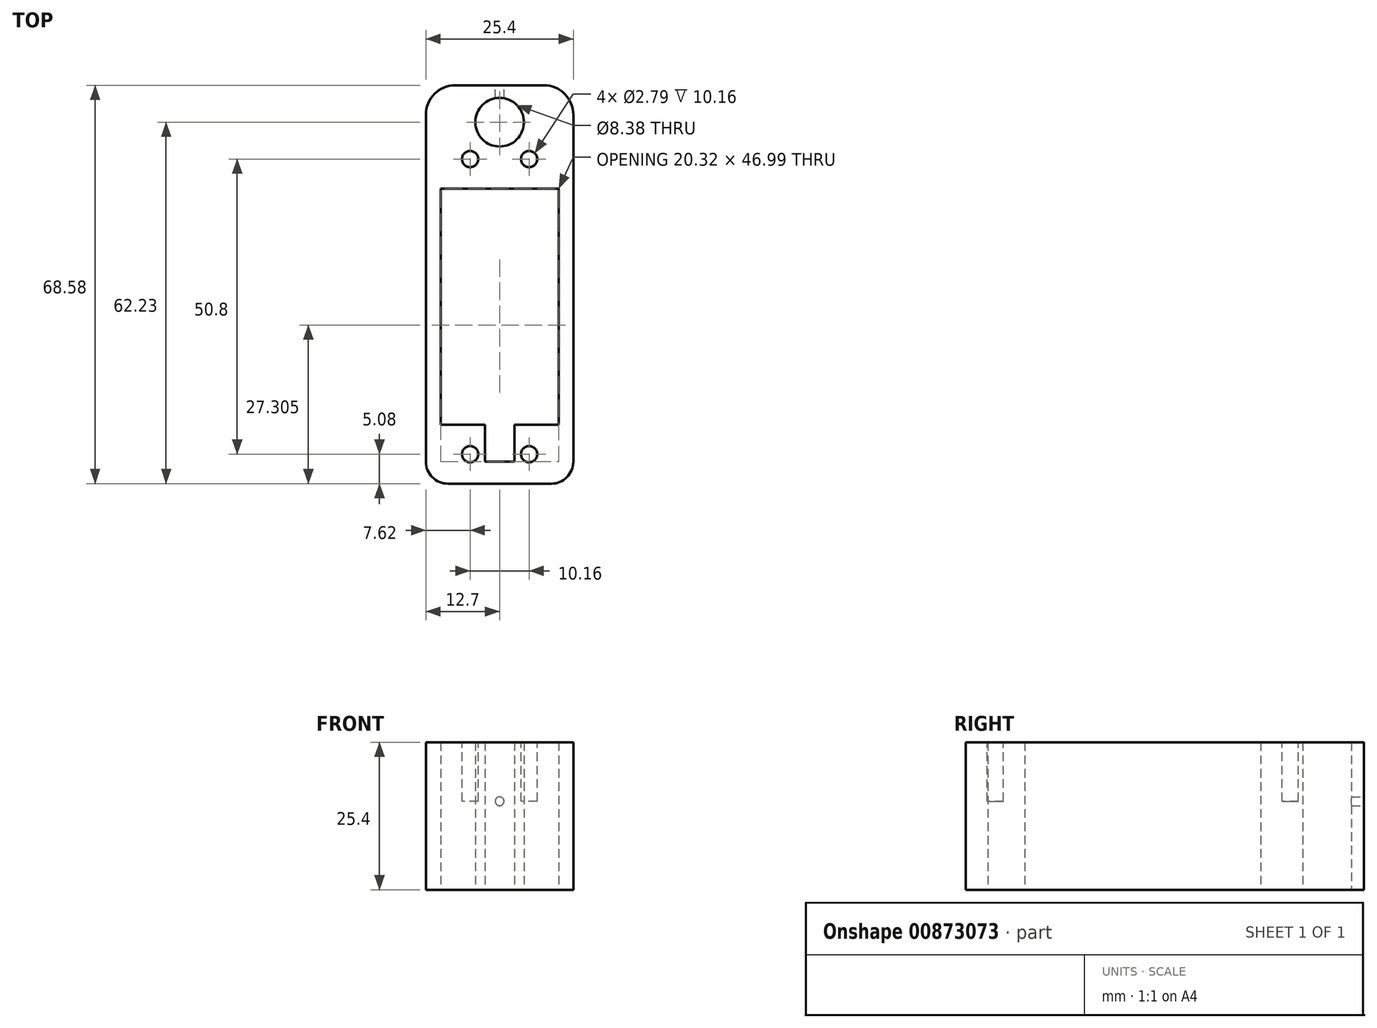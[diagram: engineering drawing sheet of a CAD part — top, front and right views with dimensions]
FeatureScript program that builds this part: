
annotation { "Feature Type Name" : "Feature", "Feature Type Description" : "" }
export const myFeature = defineFeature(function(context is Context, id is Id, definition is map)
    precondition{}
    {
        {
            var Q0;
            Q0=qCreatedBy(makeId("Top.planeOp"),FACE);
            var sketch = newSketch(context, id + "F0", { "sketchPlane" : qUnion([Q0])});
            skLineSegment(sketch, "E0.bottom", {"start": v(-10.16, 0) * mm, "end": v(10.16, 0) * mm});
            skLineSegment(sketch, "E0.top", {"start": v(-10.16, -40.64) * mm, "end": v(10.16, -40.64) * mm});
            skLineSegment(sketch, "E0.left", {"start": v(-10.16, 0) * mm, "end": v(-10.16, -40.64) * mm});
            skLineSegment(sketch, "E0.right", {"start": v(10.16, 0) * mm, "end": v(10.16, -40.64) * mm});
            skLineSegment(sketch, "E1.bottom", {"start": v(-7.62, 17.78) * mm, "end": v(7.62, 17.78) * mm});
            skLineSegment(sketch, "E1.top", {"start": v(-8.9, -50.8) * mm, "end": v(8.9, -50.8) * mm});
            skLineSegment(sketch, "E1.left", {"start": v(-12.7, 12.7) * mm, "end": v(-12.7, -47) * mm});
            skLineSegment(sketch, "E1.right", {"start": v(12.7, 12.7) * mm, "end": v(12.7, -47) * mm});
            skPoint(sketch, "E2", {"position": v(0, 11.43) * mm});
            skCircle(sketch, "E3", {"center": v(0, 11.43) * mm, "radius": 4.2 * mm});
            skPoint(sketch, "E4.visualSharp", {"position": v(-12.7, 17.78) * mm});
            skArc(sketch, "E4.filletArc", {"start": v(-7.62, 17.78) * mm, "mid": v(-11.21, 16.3) * mm, "end": v(-12.7, 12.7) * mm});
            skPoint(sketch, "E5.visualSharp", {"position": v(12.7, 17.78) * mm});
            skArc(sketch, "E5.filletArc", {"start": v(12.7, 12.7) * mm, "mid": v(11.21, 16.3) * mm, "end": v(7.62, 17.78) * mm});
            skPoint(sketch, "E6.visualSharp", {"position": v(12.7, -50.8) * mm});
            skArc(sketch, "E6.filletArc", {"start": v(8.9, -50.8) * mm, "mid": v(11.58, -49.68) * mm, "end": v(12.7, -47) * mm});
            skPoint(sketch, "E7.visualSharp", {"position": v(-12.7, -50.8) * mm});
            skArc(sketch, "E7.filletArc", {"start": v(-12.7, -47) * mm, "mid": v(-11.58, -49.68) * mm, "end": v(-8.9, -50.8) * mm});
            skLineSegment(sketch, "E8.bottom", {"start": v(-2.54, -40.64) * mm, "end": v(2.54, -40.64) * mm});
            skLineSegment(sketch, "E8.top", {"start": v(-2.54, -47) * mm, "end": v(2.54, -47) * mm});
            skLineSegment(sketch, "E8.left", {"start": v(-2.54, -40.64) * mm, "end": v(-2.54, -47) * mm});
            skLineSegment(sketch, "E8.right", {"start": v(2.54, -40.64) * mm, "end": v(2.54, -47) * mm});
            skPoint(sketch, "E9", {"position": v(0, -47) * mm});
            skSolve(sketch);
        }
        {
            var Q0;
            Q0=makeQuery(id+"F0.imprint","IMPRINT",FACE,{"disambiguationData":[TD([[makeQuery(id+"F0.imprint","IMPRINT",EDGE,{"derivedFrom":sQuery(id+"F0.wireOp",EDGE,"E0.bottom")}),1.0]])]});
            extrude(context, id + "F1", {"entities" : qUnion([Q0]), "depth" : 25.4 * mm, "offsetDistance" : 25.4 * mm});
        }
        {
            var Q0;
            Q0=makeQuery(id+"F1.opExtrude","SWEPT_FACE",FACE,{"disambiguationData":[OSD([sQuery(id+"F0.wireOp",EDGE,"E1.bottom")])]});
            var sketch = newSketch(context, id + "F2", { "sketchPlane" : qUnion([Q0])});
            skPoint(sketch, "E10", {"position": v(0, 15.24) * mm});
            skCircle(sketch, "E11", {"center": v(0, 15.24) * mm, "radius": 0.76 * mm});
            skSolve(sketch);
        }
        {
            var Q0;
            Q0=makeQuery(id+"F1.opExtrude","CAP_FACE",FACE,{"disambiguationData":[OSD([sQuery(id+"F0.wireOp",EDGE,"E0.bottom"),sQuery(id+"F0.wireOp",EDGE,"E0.top"),sQuery(id+"F0.wireOp",EDGE,"E0.left"),sQuery(id+"F0.wireOp",EDGE,"E0.right"),sQuery(id+"F0.wireOp",EDGE,"E1.bottom"),sQuery(id+"F0.wireOp",EDGE,"E1.top"),sQuery(id+"F0.wireOp",EDGE,"E1.left"),sQuery(id+"F0.wireOp",EDGE,"E1.right"),sQuery(id+"F0.wireOp",EDGE,"E3"),sQuery(id+"F0.wireOp",EDGE,"E4.filletArc"),sQuery(id+"F0.wireOp",EDGE,"E5.filletArc"),sQuery(id+"F0.wireOp",EDGE,"E6.filletArc"),sQuery(id+"F0.wireOp",EDGE,"E7.filletArc"),sQuery(id+"F0.wireOp",EDGE,"E8.top"),sQuery(id+"F0.wireOp",EDGE,"E8.left"),sQuery(id+"F0.wireOp",EDGE,"E8.right")])],"isStart":false});
            var sketch = newSketch(context, id + "F3", { "sketchPlane" : qUnion([Q0])});
            skPoint(sketch, "E12", {"position": v(-5.08, 5.08) * mm});
            skPoint(sketch, "E13", {"position": v(5.08, 5.08) * mm});
            skPoint(sketch, "E14", {"position": v(5.08, -45.72) * mm});
            skPoint(sketch, "E15", {"position": v(-5.08, -45.72) * mm});
            skCircle(sketch, "E16", {"center": v(-5.08, 5.08) * mm, "radius": 1.4 * mm});
            skCircle(sketch, "E17", {"center": v(5.08, 5.08) * mm, "radius": 1.4 * mm});
            skCircle(sketch, "E18", {"center": v(5.08, -45.72) * mm, "radius": 1.4 * mm});
            skCircle(sketch, "E19", {"center": v(-5.08, -45.72) * mm, "radius": 1.4 * mm});
            skSolve(sketch);
        }
        {
            var Q0;
            Q0 = qSketchRegion(id + "F3", true);
            extrude(context, id + "F4", {"entities" : qUnion([Q0]), "operationType" : NewBodyOperationType.REMOVE, "depth" : -10.16 * mm, "offsetDistance" : 25.4 * mm});
        }
        {
            var Q0;
            Q0 = qSketchRegion(id + "F2", true);
            extrude(context, id + "F5", {"entities" : qUnion([Q0]), "operationType" : NewBodyOperationType.REMOVE, "oppositeDirection" : true, "depth" : 5.08 * mm, "offsetDistance" : 25.4 * mm});
        }
    });
